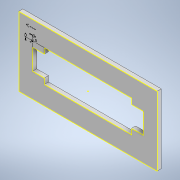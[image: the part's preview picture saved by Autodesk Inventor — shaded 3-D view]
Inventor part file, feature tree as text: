
AUTODESK INVENTOR PART (.ipt)
format: ipt  version: 2021 (Build 250183000, 183)  size: 132,608 bytes
history: native  units: mm
features: extrude x3, sketch x3, projected_geometry x1
ambient origin geometry x8: Origin, YZ Plane, XZ Plane, XY Plane, X Axis, Y Axis, Z Axis, Center Point
bodies: Solid1 (feature_tree)
feature tree (7):
  extrude  "Extrusion1"  Depth=100.0mm
  extrude  "Extrusion2"  Depth=46.0mm
  extrude  "Extrusion3"  Depth=160.0mm
  sketch  "Sketch1"  dims[d0=200.0mm d1=100.0mm]
  sketch  "Sketch2"  dims[d2=126.0mm d3=46.0mm]
  sketch  "Sketch3"  dims[d4=6.0mm d5=0.0mm d6=160.0mm d7=30.0mm d8=0.0mm d9=0.0mm d10=0.0mm d11=0.0mm d12=0.5mm d13=0.0mm d14=0.0mm]
  projected_geometry  "Projected Loop1"
